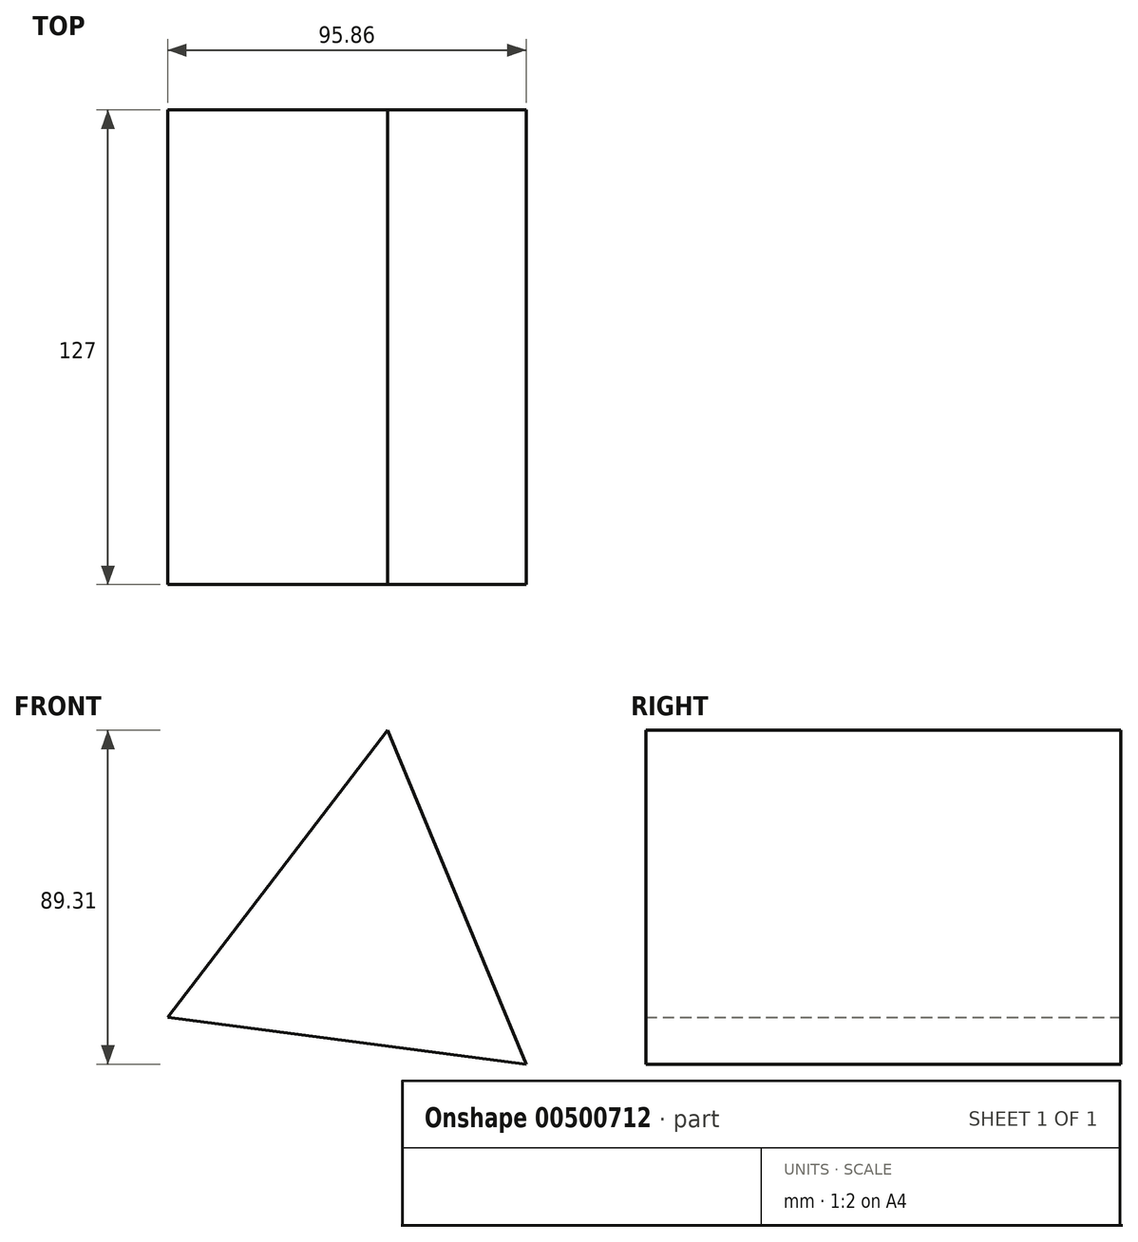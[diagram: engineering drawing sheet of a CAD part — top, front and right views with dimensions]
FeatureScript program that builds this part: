
annotation { "Feature Type Name" : "Feature", "Feature Type Description" : "" }
export const myFeature = defineFeature(function(context is Context, id is Id, definition is map)
    precondition{}
    {
        {
            var Q0;
            Q0=qCreatedBy(makeId("Front.planeOp"),FACE);
            var sketch = newSketch(context, id + "F0", { "sketchPlane" : qUnion([Q0])});
            skCircle(sketch, "E0.cCircle", {"center": v(0, 0) * mm, "radius": 55.82 * mm, "construction": true});
            skLineSegment(sketch, "E0.0", {"start": v(44.3, -33.96) * mm, "end": v(-51.56, -21.4) * mm});
            skLineSegment(sketch, "E0.1", {"start": v(-51.56, -21.4) * mm, "end": v(7.26, 55.35) * mm});
            skLineSegment(sketch, "E0.2", {"start": v(7.26, 55.35) * mm, "end": v(44.3, -33.96) * mm});
            skSolve(sketch);
        }
        {
            var Q0;
            Q0=makeQuery(id+"F0.imprint","IMPRINT",FACE,{"disambiguationData":[TD([[makeQuery(id+"F0.imprint","IMPRINT",EDGE,{"derivedFrom":sQuery(id+"F0.wireOp",EDGE,"E0.0")}),-1.0]])]});
            extrude(context, id + "F1", {"entities" : qUnion([Q0]), "depth" : 127 * mm});
        }
    });
